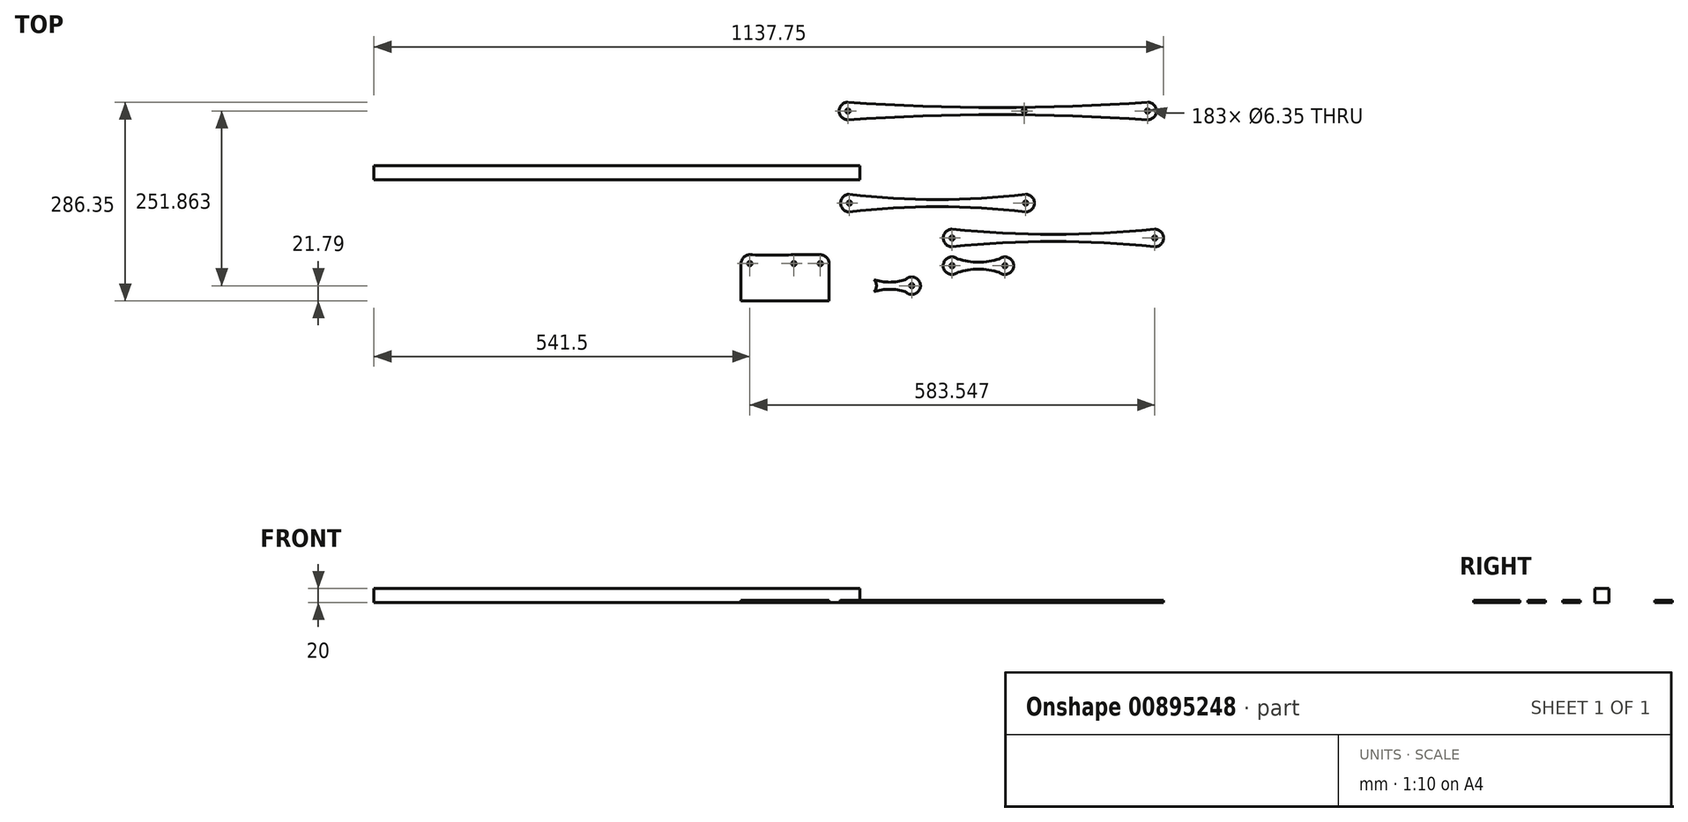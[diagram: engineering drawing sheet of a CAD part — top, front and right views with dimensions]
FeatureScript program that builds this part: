
annotation { "Feature Type Name" : "Feature", "Feature Type Description" : "" }
export const myFeature = defineFeature(function(context is Context, id is Id, definition is map)
    precondition{}
    {
        {
            var Q0;
            Q0=qCreatedBy(makeId("Top.planeOp"),FACE);
            var sketch = newSketch(context, id + "F0", { "sketchPlane" : qUnion([Q0])});
            skLineSegment(sketch, "E0.bottom", {"start": v(-57.4, 83.95) * mm, "end": v(-757.4, 83.95) * mm});
            skLineSegment(sketch, "E0.top", {"start": v(-57.4, 103.95) * mm, "end": v(-757.4, 103.95) * mm});
            skLineSegment(sketch, "E0.left", {"start": v(-57.4, 83.95) * mm, "end": v(-57.4, 103.95) * mm});
            skLineSegment(sketch, "E0.right", {"start": v(-757.4, 83.95) * mm, "end": v(-757.4, 103.95) * mm});
            skSolve(sketch);
        }
        {
            var Q0;
            Q0=qCreatedBy(makeId("Top.planeOp"),FACE);
            var sketch = newSketch(context, id + "F1", { "sketchPlane" : qUnion([Q0])});
            skCircle(sketch, "E1", {"center": v(75.55, 0) * mm, "radius": 12.7 * mm});
            skCircle(sketch, "E2", {"center": v(367.65, 0) * mm, "radius": 12.7 * mm});
            skCircle(sketch, "E3", {"center": v(75.55, 0) * mm, "radius": 3.18 * mm});
            skCircle(sketch, "E4", {"center": v(367.65, 0) * mm, "radius": 3.18 * mm});
            skArc(sketch, "E5", {"start": v(75.55, 12.7) * mm, "mid": v(221.6, 5.08) * mm, "end": v(367.65, 12.7) * mm});
            skLineSegment(sketch, "E6", {"start": v(75.55, 0) * mm, "end": v(367.65, 0) * mm});
            skArc(sketch, "E7.MirrorCS", {"start": v(75.55, -12.7) * mm, "mid": v(221.6, -5.08) * mm, "end": v(367.65, -12.7) * mm});
            skSolve(sketch);
        }
        {
            var Q0;
            Q0=qCreatedBy(makeId("Top.planeOp"),FACE);
            var sketch = newSketch(context, id + "F2", { "sketchPlane" : qUnion([Q0])});
            skCircle(sketch, "E8", {"center": v(75.55, -39.96) * mm, "radius": 12.7 * mm});
            skCircle(sketch, "E9", {"center": v(151.75, -39.96) * mm, "radius": 12.7 * mm});
            skCircle(sketch, "E10", {"center": v(75.55, -39.96) * mm, "radius": 3.18 * mm});
            skCircle(sketch, "E11", {"center": v(151.75, -39.96) * mm, "radius": 3.18 * mm});
            skArc(sketch, "E12", {"start": v(75.55, -27.26) * mm, "mid": v(113.65, -34.88) * mm, "end": v(151.75, -27.26) * mm});
            skLineSegment(sketch, "E13", {"start": v(75.55, -39.96) * mm, "end": v(151.75, -39.96) * mm});
            skArc(sketch, "E14.MirrorCS", {"start": v(75.55, -52.66) * mm, "mid": v(113.65, -45.04) * mm, "end": v(151.75, -52.66) * mm});
            skSolve(sketch);
        }
        {
            var Q0;
            Q0=qCreatedBy(makeId("Top.planeOp"),FACE);
            var sketch = newSketch(context, id + "F3", { "sketchPlane" : qUnion([Q0])});
            skCircle(sketch, "E15", {"center": v(-72.44, 50.26) * mm, "radius": 12.7 * mm});
            skCircle(sketch, "E16", {"center": v(181.56, 50.26) * mm, "radius": 12.7 * mm});
            skCircle(sketch, "E17", {"center": v(-72.44, 50.26) * mm, "radius": 3.18 * mm});
            skCircle(sketch, "E18", {"center": v(181.56, 50.26) * mm, "radius": 3.18 * mm});
            skArc(sketch, "E19", {"start": v(-72.44, 62.96) * mm, "mid": v(54.56, 55.34) * mm, "end": v(181.56, 62.96) * mm});
            skLineSegment(sketch, "E20", {"start": v(-72.44, 50.26) * mm, "end": v(181.56, 50.26) * mm});
            skArc(sketch, "E21.MirrorCS", {"start": v(-72.44, 37.56) * mm, "mid": v(54.56, 45.18) * mm, "end": v(181.56, 37.56) * mm});
            skSolve(sketch);
        }
        {
            var Q0;
            Q0=qCreatedBy(makeId("Top.planeOp"),FACE);
            var sketch = newSketch(context, id + "F4", { "sketchPlane" : qUnion([Q0])});
            skCircle(sketch, "E22", {"center": v(-74.44, 183.01) * mm, "radius": 12.7 * mm});
            skCircle(sketch, "E23", {"center": v(357.36, 183.01) * mm, "radius": 12.7 * mm});
            skCircle(sketch, "E24", {"center": v(-74.44, 183.01) * mm, "radius": 3.18 * mm});
            skCircle(sketch, "E25", {"center": v(357.36, 183.01) * mm, "radius": 3.18 * mm});
            skArc(sketch, "E26", {"start": v(-74.44, 195.71) * mm, "mid": v(141.46, 188.1) * mm, "end": v(357.36, 195.71) * mm});
            skLineSegment(sketch, "E27", {"start": v(-74.44, 183.01) * mm, "end": v(357.36, 183.01) * mm});
            skArc(sketch, "E28.MirrorCS", {"start": v(-74.44, 170.31) * mm, "mid": v(141.46, 177.93) * mm, "end": v(357.36, 170.31) * mm});
            skCircle(sketch, "E29", {"center": v(179.56, 183.01) * mm, "radius": 3.18 * mm});
            skSolve(sketch);
        }
        {
            var Q0;
            Q0=qCreatedBy(makeId("Top.planeOp"),FACE);
            var sketch = newSketch(context, id + "F5", { "sketchPlane" : qUnion([Q0])});
            skCircle(sketch, "E30", {"center": v(-46, -68.85) * mm, "radius": 12.7 * mm});
            skCircle(sketch, "E31", {"center": v(17.5, -68.85) * mm, "radius": 12.7 * mm});
            skCircle(sketch, "E32", {"center": v(-46, -68.85) * mm, "radius": 3.18 * mm});
            skCircle(sketch, "E33", {"center": v(17.5, -68.85) * mm, "radius": 3.18 * mm});
            skArc(sketch, "E34", {"start": v(-46, -56.15) * mm, "mid": v(-14.26, -63.77) * mm, "end": v(17.5, -56.15) * mm});
            skLineSegment(sketch, "E35", {"start": v(-46, -68.85) * mm, "end": v(17.5, -68.85) * mm});
            skArc(sketch, "E36.MirrorCS", {"start": v(-46, -81.55) * mm, "mid": v(-14.26, -73.93) * mm, "end": v(17.5, -81.55) * mm});
            skSolve(sketch);
        }
        {
            var Q0;
            Q0=qCreatedBy(makeId("Top.planeOp"),FACE);
            var sketch = newSketch(context, id + "F6", { "sketchPlane" : qUnion([Q0])});
            skCircle(sketch, "E37", {"center": v(-215.9, -36.96) * mm, "radius": 12.7 * mm});
            skCircle(sketch, "E38", {"center": v(-152.4, -36.96) * mm, "radius": 12.7 * mm});
            skCircle(sketch, "E39", {"center": v(-215.9, -36.96) * mm, "radius": 3.18 * mm});
            skCircle(sketch, "E40", {"center": v(-152.4, -36.96) * mm, "radius": 3.18 * mm});
            skArc(sketch, "E41", {"start": v(-215.9, -24.26) * mm, "mid": v(-184.15, -24.58) * mm, "end": v(-152.4, -24.26) * mm});
            skLineSegment(sketch, "E42.left", {"start": v(-228.6, -36.96) * mm, "end": v(-228.6, -90.64) * mm});
            skCircle(sketch, "E43", {"center": v(-114.3, -36.96) * mm, "radius": 12.7 * mm});
            skCircle(sketch, "E44", {"center": v(-114.3, -36.96) * mm, "radius": 3.18 * mm});
            skLineSegment(sketch, "E45", {"start": v(-152.4, -24.26) * mm, "end": v(-114.3, -24.26) * mm});
            skLineSegment(sketch, "E46", {"start": v(-101.6, -36.96) * mm, "end": v(-101.6, -90.64) * mm});
            skLineSegment(sketch, "E47", {"start": v(-228.6, -90.64) * mm, "end": v(-101.6, -90.64) * mm});
            skSolve(sketch);
        }
        {
            var Q0;
            {var subQ0=sQuery(id+"F1.wireOp",EDGE,"E5");var subQ1=sQuery(id+"F1.wireOp",EDGE,"E1");var subQ2=makeQuery(id+"F1.imprint","INTERSECT",VERTEX,{"disambiguationData":[OD(1.0)],"derivedFrom":[subQ1,subQ0]});Q0=makeQuery(id+"F1.imprint","IMPRINT",FACE,{"disambiguationData":[TD([[makeQuery(id+"F1.imprint","IMPRINT",EDGE,{"disambiguationData":[TD([[subQ2,1.0]])],"derivedFrom":subQ1}),-1.0]])]});}
            var Q1;
            Q1=makeQuery(id+"F1.imprint","IMPRINT",FACE,{"disambiguationData":[TD([[makeQuery(id+"F1.imprint","IMPRINT",EDGE,{"derivedFrom":sQuery(id+"F1.wireOp",EDGE,"E3")}),-1.0]])]});
            var Q2;
            {var subQ0=sQuery(id+"F1.wireOp",EDGE,"E6");var subQ1=sQuery(id+"F1.wireOp",EDGE,"E1");var subQ2=makeQuery(id+"F1.imprint","INTERSECT",VERTEX,{"derivedFrom":[subQ1,subQ0]});Q2=makeQuery(id+"F1.imprint","IMPRINT",FACE,{"disambiguationData":[TD([[makeQuery(id+"F1.imprint","IMPRINT",EDGE,{"disambiguationData":[TD([[subQ2,1.0]])],"derivedFrom":subQ1}),-1.0]])]});}
            var Q3;
            Q3=makeQuery(id+"F1.imprint","IMPRINT",FACE,{"disambiguationData":[TD([[makeQuery(id+"F1.imprint","IMPRINT",EDGE,{"derivedFrom":sQuery(id+"F1.wireOp",EDGE,"E4")}),-1.0]])]});
            extrude(context, id + "F7", {"entities" : qUnion([Q0, Q1, Q2, Q3]), "depth" : 3.17 * mm});
        }
        {
            var Q0;
            {var subQ0=sQuery(id+"F2.wireOp",EDGE,"E12");var subQ1=sQuery(id+"F2.wireOp",EDGE,"E8");var subQ2=makeQuery(id+"F2.imprint","INTERSECT",VERTEX,{"disambiguationData":[OD(1.0)],"derivedFrom":[subQ1,subQ0]});Q0=makeQuery(id+"F2.imprint","IMPRINT",FACE,{"disambiguationData":[TD([[makeQuery(id+"F2.imprint","IMPRINT",EDGE,{"disambiguationData":[TD([[subQ2,1.0]])],"derivedFrom":subQ1}),-1.0]])]});}
            var Q1;
            Q1=makeQuery(id+"F2.imprint","IMPRINT",FACE,{"disambiguationData":[TD([[makeQuery(id+"F2.imprint","IMPRINT",EDGE,{"derivedFrom":sQuery(id+"F2.wireOp",EDGE,"E11")}),-1.0]])]});
            var Q2;
            {var subQ0=sQuery(id+"F2.wireOp",EDGE,"E13");var subQ1=sQuery(id+"F2.wireOp",EDGE,"E8");var subQ2=makeQuery(id+"F2.imprint","INTERSECT",VERTEX,{"derivedFrom":[subQ1,subQ0]});Q2=makeQuery(id+"F2.imprint","IMPRINT",FACE,{"disambiguationData":[TD([[makeQuery(id+"F2.imprint","IMPRINT",EDGE,{"disambiguationData":[TD([[subQ2,1.0]])],"derivedFrom":subQ1}),-1.0]])]});}
            var Q3;
            {var subQ0=sQuery(id+"F2.wireOp",EDGE,"E14.MirrorCS");var subQ1=sQuery(id+"F2.wireOp",EDGE,"E8");var subQ2=makeQuery(id+"F2.imprint","INTERSECT",VERTEX,{"disambiguationData":[OD(0.0)],"derivedFrom":[subQ1,subQ0]});Q3=makeQuery(id+"F2.imprint","IMPRINT",FACE,{"disambiguationData":[TD([[makeQuery(id+"F2.imprint","IMPRINT",EDGE,{"disambiguationData":[TD([[subQ2,-1.0]])],"derivedFrom":subQ1}),1.0]])]});}
            var Q4;
            {var subQ0=sQuery(id+"F2.wireOp",EDGE,"E14.MirrorCS");var subQ1=sQuery(id+"F2.wireOp",EDGE,"E9");var subQ2=makeQuery(id+"F2.imprint","INTERSECT",VERTEX,{"disambiguationData":[OD(0.0)],"derivedFrom":[subQ1,subQ0]});Q4=makeQuery(id+"F2.imprint","IMPRINT",FACE,{"disambiguationData":[TD([[makeQuery(id+"F2.imprint","IMPRINT",EDGE,{"disambiguationData":[TD([[subQ2,1.0]])],"derivedFrom":subQ1}),1.0]])]});}
            var Q5;
            Q5=makeQuery(id+"F2.imprint","IMPRINT",FACE,{"disambiguationData":[TD([[makeQuery(id+"F2.imprint","IMPRINT",EDGE,{"derivedFrom":sQuery(id+"F2.wireOp",EDGE,"E10")}),-1.0]])]});
            var Q6;
            {var subQ0=sQuery(id+"F2.wireOp",EDGE,"E12");var subQ1=sQuery(id+"F2.wireOp",EDGE,"E8");var subQ2=makeQuery(id+"F2.imprint","INTERSECT",VERTEX,{"disambiguationData":[OD(0.0)],"derivedFrom":[subQ1,subQ0]});Q6=makeQuery(id+"F2.imprint","IMPRINT",FACE,{"disambiguationData":[TD([[makeQuery(id+"F2.imprint","IMPRINT",EDGE,{"disambiguationData":[TD([[subQ2,1.0]])],"derivedFrom":subQ1}),1.0]])]});}
            var Q7;
            {var subQ0=sQuery(id+"F2.wireOp",EDGE,"E12");var subQ1=sQuery(id+"F2.wireOp",EDGE,"E9");var subQ2=makeQuery(id+"F2.imprint","INTERSECT",VERTEX,{"disambiguationData":[OD(0.0)],"derivedFrom":[subQ1,subQ0]});Q7=makeQuery(id+"F2.imprint","IMPRINT",FACE,{"disambiguationData":[TD([[makeQuery(id+"F2.imprint","IMPRINT",EDGE,{"disambiguationData":[TD([[subQ2,-1.0]])],"derivedFrom":subQ1}),1.0]])]});}
            extrude(context, id + "F8", {"entities" : qUnion([Q0, Q1, Q2, Q3, Q4, Q5, Q6, Q7]), "depth" : 3.17 * mm});
        }
        {
            var Q0;
            {var subQ0=sQuery(id+"F5.wireOp",EDGE,"E34");var subQ1=sQuery(id+"F5.wireOp",EDGE,"E30");var subQ2=makeQuery(id+"F5.imprint","INTERSECT",VERTEX,{"disambiguationData":[OD(1.0)],"derivedFrom":[subQ1,subQ0]});Q0=makeQuery(id+"F5.imprint","IMPRINT",FACE,{"disambiguationData":[TD([[makeQuery(id+"F5.imprint","IMPRINT",EDGE,{"disambiguationData":[TD([[subQ2,1.0]])],"derivedFrom":subQ1}),-1.0]])]});}
            var Q1;
            {var subQ0=sQuery(id+"F5.wireOp",EDGE,"E35");var subQ1=sQuery(id+"F5.wireOp",EDGE,"E30");var subQ2=makeQuery(id+"F5.imprint","INTERSECT",VERTEX,{"derivedFrom":[subQ1,subQ0]});Q1=makeQuery(id+"F5.imprint","IMPRINT",FACE,{"disambiguationData":[TD([[makeQuery(id+"F5.imprint","IMPRINT",EDGE,{"disambiguationData":[TD([[subQ2,1.0]])],"derivedFrom":subQ1}),-1.0]])]});}
            var Q2;
            Q2=makeQuery(id+"F5.imprint","IMPRINT",FACE,{"disambiguationData":[TD([[makeQuery(id+"F5.imprint","IMPRINT",EDGE,{"derivedFrom":sQuery(id+"F5.wireOp",EDGE,"E33")}),-1.0]])]});
            var Q3;
            {var subQ0=sQuery(id+"F5.wireOp",EDGE,"E36.MirrorCS");var subQ1=sQuery(id+"F5.wireOp",EDGE,"E31");var subQ2=makeQuery(id+"F5.imprint","INTERSECT",VERTEX,{"disambiguationData":[OD(0.0)],"derivedFrom":[subQ1,subQ0]});Q3=makeQuery(id+"F5.imprint","IMPRINT",FACE,{"disambiguationData":[TD([[makeQuery(id+"F5.imprint","IMPRINT",EDGE,{"disambiguationData":[TD([[subQ2,1.0]])],"derivedFrom":subQ1}),1.0]])]});}
            var Q4;
            {var subQ0=sQuery(id+"F5.wireOp",EDGE,"E34");var subQ1=sQuery(id+"F5.wireOp",EDGE,"E31");var subQ2=makeQuery(id+"F5.imprint","INTERSECT",VERTEX,{"disambiguationData":[OD(0.0)],"derivedFrom":[subQ1,subQ0]});Q4=makeQuery(id+"F5.imprint","IMPRINT",FACE,{"disambiguationData":[TD([[makeQuery(id+"F5.imprint","IMPRINT",EDGE,{"disambiguationData":[TD([[subQ2,-1.0]])],"derivedFrom":subQ1}),1.0]])]});}
            extrude(context, id + "F9", {"entities" : qUnion([Q0, Q1, Q2, Q3, Q4]), "depth" : 3.17 * mm});
        }
        {
            var Q0;
            {var subQ0=sQuery(id+"F6.wireOp",EDGE,"E41");var subQ1=sQuery(id+"F6.wireOp",EDGE,"E37");var subQ3=makeQuery(id+"F6.imprint","INTERSECT",VERTEX,{"disambiguationData":[OD(1.0)],"derivedFrom":[subQ1,subQ0]});Q0=makeQuery(id+"F6.imprint","IMPRINT",FACE,{"disambiguationData":[TD([[makeQuery(id+"F6.imprint","IMPRINT",EDGE,{"disambiguationData":[TD([[subQ3,1.0]])],"derivedFrom":subQ1}),1.0]])]});}
            var Q1;
            {var subQ0=sQuery(id+"F6.wireOp",EDGE,"E41");var subQ1=sQuery(id+"F6.wireOp",EDGE,"E37");var subQ2=makeQuery(id+"F6.imprint","INTERSECT",VERTEX,{"disambiguationData":[OD(1.0)],"derivedFrom":[subQ1,subQ0]});Q1=makeQuery(id+"F6.imprint","IMPRINT",FACE,{"disambiguationData":[TD([[makeQuery(id+"F6.imprint","IMPRINT",EDGE,{"disambiguationData":[TD([[subQ2,1.0]])],"derivedFrom":subQ1}),-1.0]])]});}
            var Q2;
            {var subQ0=sQuery(id+"F6.wireOp",EDGE,"E41");var subQ1=sQuery(id+"F6.wireOp",EDGE,"E38");var subQ3=makeQuery(id+"F6.imprint","INTERSECT",VERTEX,{"disambiguationData":[OD(1.0)],"derivedFrom":[subQ1,subQ0]});Q2=makeQuery(id+"F6.imprint","IMPRINT",FACE,{"disambiguationData":[TD([[makeQuery(id+"F6.imprint","IMPRINT",EDGE,{"disambiguationData":[TD([[subQ3,-1.0]])],"derivedFrom":subQ1}),1.0]])]});}
            var Q3;
            {var subQ0=sQuery(id+"F6.wireOp",EDGE,"E42.bottom");var subQ4=sQuery(id+"F6.wireOp",EDGE,"E40");var subQ5=makeQuery(id+"F6.imprint","INTERSECT",VERTEX,{"disambiguationData":[OD(0.0)],"derivedFrom":[subQ4,subQ0]});Q3=makeQuery(id+"F6.imprint","IMPRINT",FACE,{"disambiguationData":[TD([[makeQuery(id+"F6.imprint","IMPRINT",EDGE,{"disambiguationData":[TD([[subQ5,-1.0]])],"derivedFrom":subQ4}),-1.0]])]});}
            var Q4;
            {var subQ0=sQuery(id+"F6.wireOp",EDGE,"E42.bottom");var subQ4=sQuery(id+"F6.wireOp",EDGE,"E39");var subQ5=makeQuery(id+"F6.imprint","INTERSECT",VERTEX,{"disambiguationData":[OD(0.0)],"derivedFrom":[subQ4,subQ0]});Q4=makeQuery(id+"F6.imprint","IMPRINT",FACE,{"disambiguationData":[TD([[makeQuery(id+"F6.imprint","IMPRINT",EDGE,{"disambiguationData":[TD([[subQ5,-1.0]])],"derivedFrom":subQ4}),-1.0]])]});}
            var Q5;
            Q5=makeQuery(id+"F6.imprint","IMPRINT",FACE,{"disambiguationData":[TD([[makeQuery(id+"F6.imprint","IMPRINT",EDGE,{"derivedFrom":sQuery(id+"F6.wireOp",EDGE,"E42.top")}),1.0]])]});
            var Q6;
            Q6=makeQuery(id+"F6.imprint","IMPRINT",FACE,{"disambiguationData":[TD([[makeQuery(id+"F6.imprint","IMPRINT",EDGE,{"derivedFrom":sQuery(id+"F6.wireOp",EDGE,"E44")}),-1.0]])]});
            extrude(context, id + "F10", {"entities" : qUnion([Q0, Q1, Q2, Q3, Q4, Q5, Q6]), "operationType" : NewBodyOperationType.ADD, "depth" : 3.17 * mm});
        }
        {
            var Q0;
            Q0=makeQuery(id+"F3.imprint","IMPRINT",FACE,{"disambiguationData":[TD([[makeQuery(id+"F3.imprint","IMPRINT",EDGE,{"derivedFrom":sQuery(id+"F3.wireOp",EDGE,"E17")}),-1.0]])]});
            var Q1;
            {var subQ0=sQuery(id+"F3.wireOp",EDGE,"E19");var subQ1=sQuery(id+"F3.wireOp",EDGE,"E15");var subQ2=makeQuery(id+"F3.imprint","INTERSECT",VERTEX,{"disambiguationData":[OD(1.0)],"derivedFrom":[subQ1,subQ0]});Q1=makeQuery(id+"F3.imprint","IMPRINT",FACE,{"disambiguationData":[TD([[makeQuery(id+"F3.imprint","IMPRINT",EDGE,{"disambiguationData":[TD([[subQ2,1.0]])],"derivedFrom":subQ1}),-1.0]])]});}
            var Q2;
            {var subQ0=sQuery(id+"F3.wireOp",EDGE,"E20");var subQ1=sQuery(id+"F3.wireOp",EDGE,"E15");var subQ2=makeQuery(id+"F3.imprint","INTERSECT",VERTEX,{"derivedFrom":[subQ1,subQ0]});Q2=makeQuery(id+"F3.imprint","IMPRINT",FACE,{"disambiguationData":[TD([[makeQuery(id+"F3.imprint","IMPRINT",EDGE,{"disambiguationData":[TD([[subQ2,1.0]])],"derivedFrom":subQ1}),-1.0]])]});}
            var Q3;
            Q3=makeQuery(id+"F3.imprint","IMPRINT",FACE,{"disambiguationData":[TD([[makeQuery(id+"F3.imprint","IMPRINT",EDGE,{"derivedFrom":sQuery(id+"F3.wireOp",EDGE,"E18")}),-1.0]])]});
            extrude(context, id + "F11", {"entities" : qUnion([Q0, Q1, Q2, Q3]), "depth" : 3.17 * mm});
        }
        {
            var Q0;
            Q0=makeQuery(id+"F4.imprint","IMPRINT",FACE,{"disambiguationData":[TD([[makeQuery(id+"F4.imprint","IMPRINT",EDGE,{"derivedFrom":sQuery(id+"F4.wireOp",EDGE,"E24")}),-1.0]])]});
            var Q1;
            {var subQ1=sQuery(id+"F4.wireOp",EDGE,"E22");var subQ5=sQuery(id+"F4.wireOp",EDGE,"E26");var subQ6=makeQuery(id+"F4.imprint","INTERSECT",VERTEX,{"disambiguationData":[OD(1.0)],"derivedFrom":[subQ1,subQ5]});Q1=makeQuery(id+"F4.imprint","IMPRINT",FACE,{"disambiguationData":[TD([[makeQuery(id+"F4.imprint","IMPRINT",EDGE,{"disambiguationData":[TD([[subQ6,1.0]])],"derivedFrom":subQ1}),-1.0]])]});}
            var Q2;
            {var subQ0=sQuery(id+"F4.wireOp",EDGE,"E27");var subQ5=sQuery(id+"F4.wireOp",EDGE,"E22");var subQ6=makeQuery(id+"F4.imprint","INTERSECT",VERTEX,{"derivedFrom":[subQ5,subQ0]});Q2=makeQuery(id+"F4.imprint","IMPRINT",FACE,{"disambiguationData":[TD([[makeQuery(id+"F4.imprint","IMPRINT",EDGE,{"disambiguationData":[TD([[subQ6,1.0]])],"derivedFrom":subQ5}),-1.0]])]});}
            var Q3;
            Q3=makeQuery(id+"F4.imprint","IMPRINT",FACE,{"disambiguationData":[TD([[makeQuery(id+"F4.imprint","IMPRINT",EDGE,{"derivedFrom":sQuery(id+"F4.wireOp",EDGE,"E25")}),-1.0]])]});
            extrude(context, id + "F12", {"entities" : qUnion([Q0, Q1, Q2, Q3]), "depth" : 3.17 * mm});
        }
        {
            var Q0;
            Q0=makeQuery(id+"F0.imprint","IMPRINT",FACE,{"disambiguationData":[TD([[makeQuery(id+"F0.imprint","IMPRINT",EDGE,{"derivedFrom":sQuery(id+"F0.wireOp",EDGE,"E0.bottom")}),-1.0]])]});
            extrude(context, id + "F13", {"entities" : qUnion([Q0]), "depth" : 20 * mm});
        }
    });
